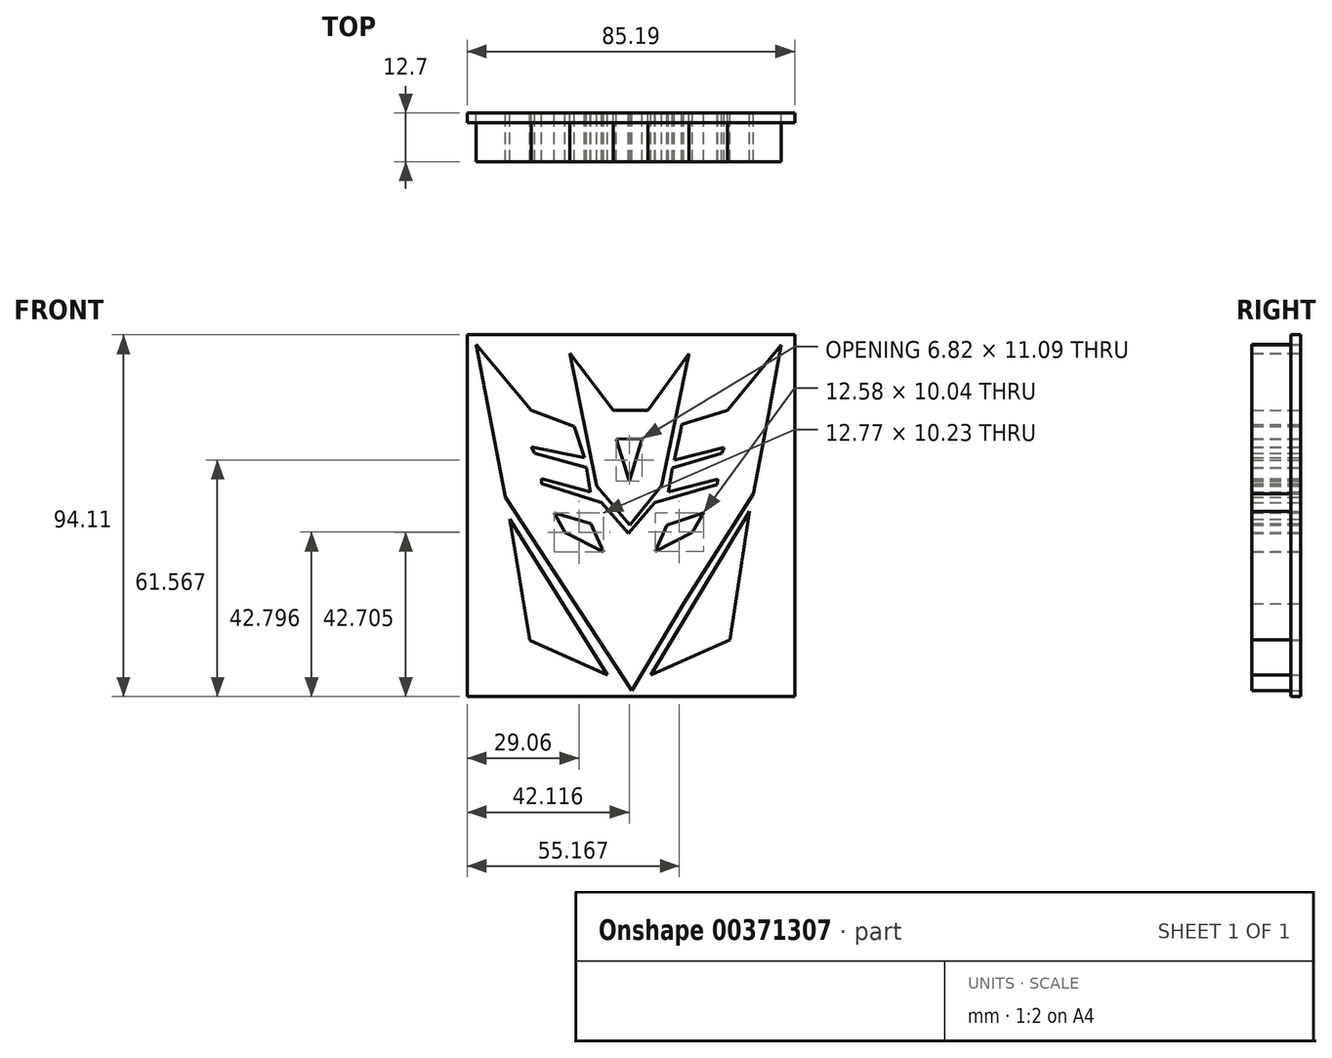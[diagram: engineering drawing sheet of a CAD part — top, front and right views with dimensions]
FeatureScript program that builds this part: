
annotation { "Feature Type Name" : "Feature", "Feature Type Description" : "" }
export const myFeature = defineFeature(function(context is Context, id is Id, definition is map)
    precondition{}
    {
        {
            var Q0;
            Q0=qCreatedBy(makeId("Front.planeOp"),FACE);
            var sketch = newSketch(context, id + "F0", { "sketchPlane" : qUnion([Q0])});
            skLineSegment(sketch, "E0", {"start": v(-40.6, 56.55) * mm, "end": v(-26.17, 39.4) * mm});
            skLineSegment(sketch, "E1", {"start": v(-15.04, 35.2) * mm, "end": v(-26.17, 39.4) * mm});
            skLineSegment(sketch, "E2", {"start": v(-15.04, 35.2) * mm, "end": v(-12.33, 27.07) * mm});
            skLineSegment(sketch, "E3", {"start": v(-26.17, 29.78) * mm, "end": v(-12.33, 27.07) * mm});
            skLineSegment(sketch, "E4", {"start": v(-26.17, 29.78) * mm, "end": v(-25.34, 28.14) * mm});
            skLineSegment(sketch, "E5", {"start": v(-25.34, 28.14) * mm, "end": v(-11.88, 24.52) * mm});
            skLineSegment(sketch, "E6", {"start": v(-11.88, 24.52) * mm, "end": v(-10.86, 18.12) * mm});
            skLineSegment(sketch, "E7", {"start": v(-10.86, 18.12) * mm, "end": v(-23.55, 21.61) * mm});
            skLineSegment(sketch, "E8", {"start": v(-23.55, 21.61) * mm, "end": v(-23.55, 20.27) * mm});
            skLineSegment(sketch, "E9", {"start": v(-23.55, 20.27) * mm, "end": v(-7.9, 15.35) * mm});
            skLineSegment(sketch, "E10", {"start": v(-7.9, 15.35) * mm, "end": v(-1, 7.31) * mm});
            skLineSegment(sketch, "E11", {"start": v(-1, 7.31) * mm, "end": v(5.89, 15.35) * mm});
            skLineSegment(sketch, "E12", {"start": v(5.89, 15.35) * mm, "end": v(22.16, 20.01) * mm});
            skLineSegment(sketch, "E13", {"start": v(22.16, 20.01) * mm, "end": v(22.32, 21.46) * mm});
            skLineSegment(sketch, "E14", {"start": v(22.32, 21.46) * mm, "end": v(9.5, 18.09) * mm});
            skLineSegment(sketch, "E15", {"start": v(9.5, 18.09) * mm, "end": v(10.51, 24.4) * mm});
            skLineSegment(sketch, "E16", {"start": v(10.51, 24.4) * mm, "end": v(23.35, 28.12) * mm});
            skLineSegment(sketch, "E17", {"start": v(23.35, 28.12) * mm, "end": v(23.95, 29.7) * mm});
            skLineSegment(sketch, "E18", {"start": v(23.95, 29.7) * mm, "end": v(10.98, 26.4) * mm});
            skLineSegment(sketch, "E19", {"start": v(10.98, 26.4) * mm, "end": v(12.6, 34.06) * mm});
            skLineSegment(sketch, "E20", {"start": v(12.6, 34.06) * mm, "end": v(12.93, 35.64) * mm});
            skLineSegment(sketch, "E21", {"start": v(12.93, 35.64) * mm, "end": v(12.6, 34.06) * mm});
            skLineSegment(sketch, "E22", {"start": v(12.93, 35.64) * mm, "end": v(24.77, 39.36) * mm});
            skLineSegment(sketch, "E23", {"start": v(24.77, 39.36) * mm, "end": v(32.8, 49.1) * mm});
            skLineSegment(sketch, "E24", {"start": v(32.8, 49.1) * mm, "end": v(38.83, 56.42) * mm});
            skLineSegment(sketch, "E25", {"start": v(38.83, 56.42) * mm, "end": v(35.44, 38.24) * mm});
            skLineSegment(sketch, "E26", {"start": v(35.44, 38.24) * mm, "end": v(31.56, 17.68) * mm});
            skLineSegment(sketch, "E27", {"start": v(31.56, 17.68) * mm, "end": v(13.4, -10.97) * mm});
            skLineSegment(sketch, "E28", {"start": v(13.4, -10.97) * mm, "end": v(0, -33.58) * mm});
            skLineSegment(sketch, "E29", {"start": v(-32.9, 16.8) * mm, "end": v(0, -33.58) * mm});
            skLineSegment(sketch, "E30", {"start": v(-40.6, 56.55) * mm, "end": v(-32.9, 16.8) * mm});
            skLineSegment(sketch, "E31", {"start": v(30.56, 13.1) * mm, "end": v(4.82, -29.44) * mm});
            skLineSegment(sketch, "E32", {"start": v(30.56, 13.1) * mm, "end": v(25.45, -20.3) * mm});
            skLineSegment(sketch, "E33", {"start": v(25.45, -20.3) * mm, "end": v(4.82, -29.44) * mm});
            skLineSegment(sketch, "E34", {"start": v(-32.18, 13.1) * mm, "end": v(-26.65, -20.5) * mm});
            skLineSegment(sketch, "E35", {"start": v(-26.65, -20.5) * mm, "end": v(-6.45, -29.44) * mm});
            skLineSegment(sketch, "E36", {"start": v(-6.45, -29.44) * mm, "end": v(-31.86, 11.1) * mm});
            skLineSegment(sketch, "E37", {"start": v(-20.2, 12.7) * mm, "end": v(-10.7, 9.86) * mm});
            skLineSegment(sketch, "E38", {"start": v(-10.7, 9.86) * mm, "end": v(-7.44, 2.48) * mm});
            skLineSegment(sketch, "E39", {"start": v(-7.44, 2.48) * mm, "end": v(-17.42, 7.56) * mm});
            skLineSegment(sketch, "E40", {"start": v(-17.42, 7.56) * mm, "end": v(-20.2, 12.7) * mm});
            skLineSegment(sketch, "E41", {"start": v(6, 2.66) * mm, "end": v(9.02, 9.5) * mm});
            skLineSegment(sketch, "E42", {"start": v(9.02, 9.5) * mm, "end": v(18.58, 12.7) * mm});
            skLineSegment(sketch, "E43", {"start": v(18.58, 12.7) * mm, "end": v(15.74, 7.56) * mm});
            skLineSegment(sketch, "E44", {"start": v(15.74, 7.56) * mm, "end": v(6, 2.66) * mm});
            skLineSegment(sketch, "E45", {"start": v(-0.63, 9.53) * mm, "end": v(7.71, 19.78) * mm});
            skPoint(sketch, "E45.endSnap0", {"position": v(15.91, 19.78) * mm});
            skLineSegment(sketch, "E46", {"start": v(7.71, 19.78) * mm, "end": v(10, 30.66) * mm});
            skLineSegment(sketch, "E47", {"start": v(10, 30.66) * mm, "end": v(14.86, 54.08) * mm});
            skLineSegment(sketch, "E48", {"start": v(14.86, 54.08) * mm, "end": v(4.07, 39.33) * mm});
            skLineSegment(sketch, "E49", {"start": v(4.07, 39.33) * mm, "end": v(-4.89, 39.33) * mm});
            skLineSegment(sketch, "E50", {"start": v(-4.89, 39.33) * mm, "end": v(-16.18, 54.19) * mm});
            skLineSegment(sketch, "E51", {"start": v(-16.18, 54.19) * mm, "end": v(-9.26, 19.7) * mm});
            skLineSegment(sketch, "E52", {"start": v(-9.26, 19.7) * mm, "end": v(-0.63, 9.53) * mm});
            skLineSegment(sketch, "E53", {"start": v(-0.71, 20.91) * mm, "end": v(2.64, 32) * mm});
            skLineSegment(sketch, "E54", {"start": v(2.64, 32) * mm, "end": v(-4.17, 31.9) * mm});
            skLineSegment(sketch, "E55", {"start": v(-4.17, 31.9) * mm, "end": v(-0.71, 20.91) * mm});
            skSolve(sketch);
        }
        {
            var Q0;
            Q0 = qSketchRegion(id + "F0", true);
            extrude(context, id + "F1", {"entities" : qUnion([Q0]), "depth" : 12.7 * mm});
        }
        {
            var Q0;
            Q0=qCreatedBy(makeId("Front.planeOp"),FACE);
            var sketch = newSketch(context, id + "F2", { "sketchPlane" : qUnion([Q0])});
            skLineSegment(sketch, "E56.bottom", {"start": v(42.3, 59) * mm, "end": v(-42.88, 59) * mm});
            skLineSegment(sketch, "E56.top", {"start": v(42.3, -35.11) * mm, "end": v(-42.88, -35.11) * mm});
            skLineSegment(sketch, "E56.left", {"start": v(42.3, 59) * mm, "end": v(42.3, -35.11) * mm});
            skLineSegment(sketch, "E56.right", {"start": v(-42.88, 59) * mm, "end": v(-42.88, -35.11) * mm});
            skSolve(sketch);
        }
        {
            var Q0;
            Q0 = qSketchRegion(id + "F2", true);
            extrude(context, id + "F3", {"entities" : qUnion([Q0]), "depth" : 2.54 * mm});
        }
    });
